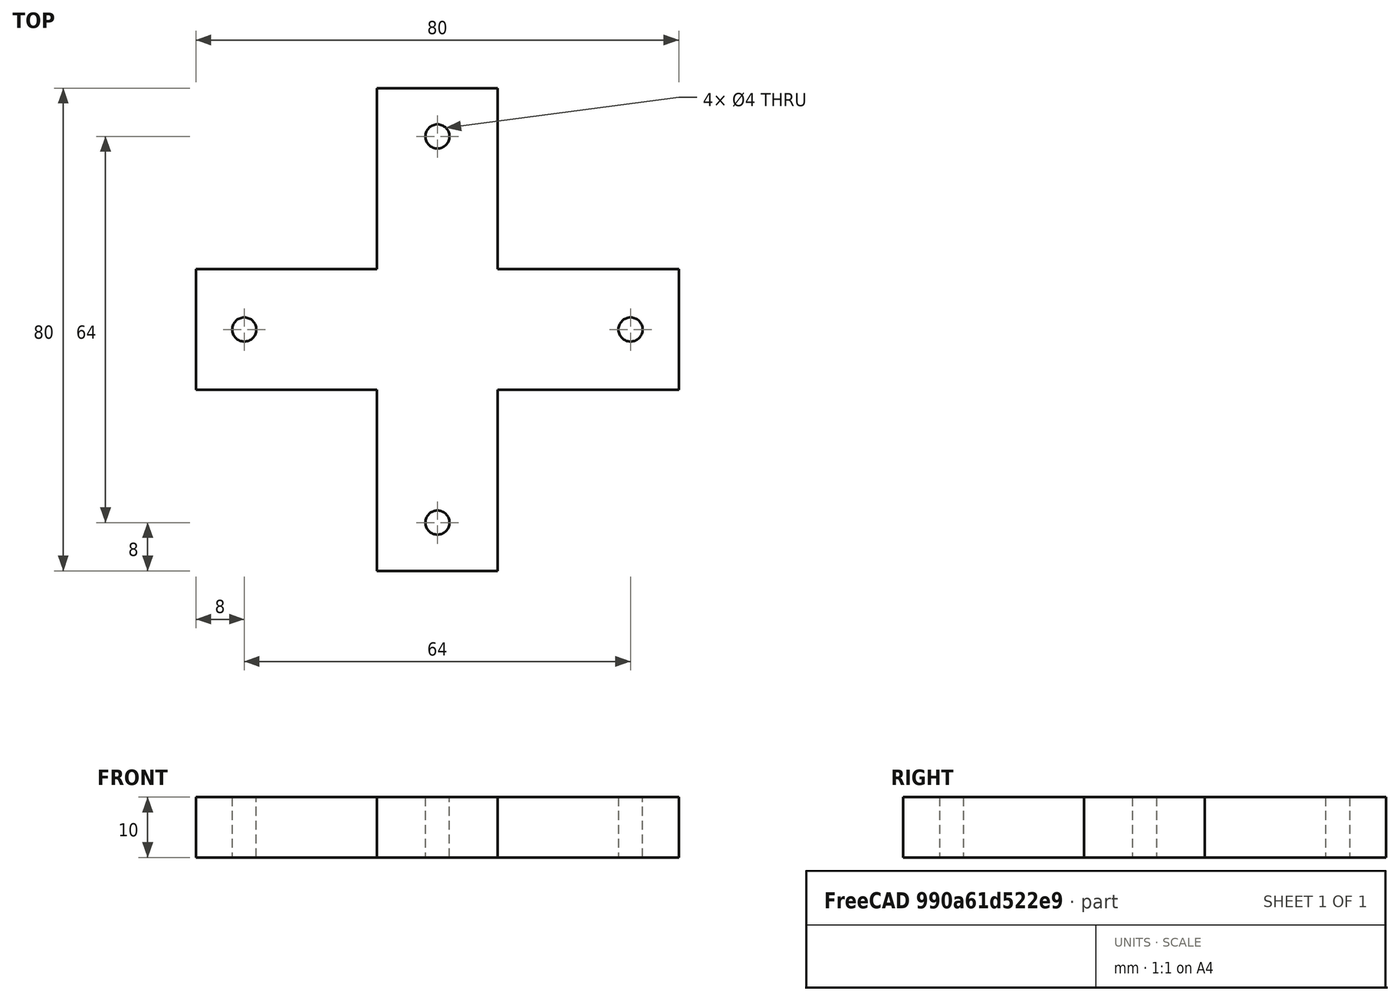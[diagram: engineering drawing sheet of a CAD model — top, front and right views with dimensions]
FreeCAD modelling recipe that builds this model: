
FCSTD DOCUMENT  (FreeCAD 0.21R33694 (Git))
Label: OJT1_T19R02.alf
License: All rights reserved
LicenseURL: http://en.wikipedia.org/wiki/All_rights_reserved
objects: Sketcher::SketchObject×1, PartDesign::Pad×1, PartDesign::Body×1, App::Part×1
note: 4 computed .brp shape members not serialized (recipe doc carries the construction recipe); baked Part::Feature solids carry a one-line shape summary decoded from their .brp

FEATURE [Sketcher::SketchObject] Sketch
  FullyConstrained = true
  MapMode = 5
  Support = -> [XY_Plane001]
  sketch-geometry (16):
    g0: LineSegment StartX=-10 StartY=40 StartZ=0 EndX=10 EndY=40 EndZ=0
    g1: LineSegment StartX=10 StartY=40 StartZ=0 EndX=10 EndY=10 EndZ=0
    g2: LineSegment StartX=10 StartY=10 StartZ=0 EndX=40 EndY=10 EndZ=0
    g3: LineSegment StartX=40 StartY=10 StartZ=0 EndX=40 EndY=-10 EndZ=0
    g4: LineSegment StartX=40 StartY=-10 StartZ=0 EndX=10 EndY=-10 EndZ=0
    g5: LineSegment StartX=10 StartY=-10 StartZ=0 EndX=10 EndY=-40 EndZ=0
    g6: LineSegment StartX=10 StartY=-40 StartZ=0 EndX=-10 EndY=-40 EndZ=0
    g7: LineSegment StartX=-10 StartY=-40 StartZ=0 EndX=-10 EndY=-10 EndZ=0
    g8: LineSegment StartX=-10 StartY=-10 StartZ=0 EndX=-40 EndY=-10 EndZ=0
    g9: LineSegment StartX=-40 StartY=-10 StartZ=0 EndX=-40 EndY=10 EndZ=0
    g10: LineSegment StartX=-40 StartY=10 StartZ=0 EndX=-10 EndY=10 EndZ=0
    g11: LineSegment StartX=-10 StartY=10 StartZ=0 EndX=-10 EndY=40 EndZ=0
    g12: Circle CenterX=0 CenterY=32 CenterZ=0 NormalX=0 NormalY=0 NormalZ=1 AngleXU=0 Radius=2
    g13: Circle CenterX=32 CenterY=0 CenterZ=0 NormalX=0 NormalY=0 NormalZ=1 AngleXU=0 Radius=2
    g14: Circle CenterX=0 CenterY=-32 CenterZ=0 NormalX=0 NormalY=0 NormalZ=1 AngleXU=0 Radius=2
    g15: Circle CenterX=-32 CenterY=0 CenterZ=0 NormalX=0 NormalY=0 NormalZ=1 AngleXU=0 Radius=2
  constraints (45):
    c: Horizontal(g0)
    c: Coincident(g0,g1)
    c: Vertical(g1)
    c: Coincident(g1,g2)
    c: Horizontal(g2)
    c: Coincident(g2,g3)
    c: Vertical(g3)
    c: Coincident(g3,g4)
    c: Coincident(g4,g5)
    c: Vertical(g5)
    c: Coincident(g5,g6)
    c: Horizontal(g6)
    c: Coincident(g6,g7)
    c: Vertical(g7)
    c: Coincident(g7,g8)
    c: Coincident(g8,g9)
    c: Vertical(g9)
    c: Coincident(g9,g10)
    c: Coincident(g10,g11)
    c: Coincident(g11,g0)
    c: Vertical(g11)
    c: Horizontal(g4)
    c: Horizontal(g8)
    c: Horizontal(g10)
    c: Symmetric(g4,g7,g-2)
    c: Distance(g3,g8) = 80
    c: Distance(g6,g5) = 20
    c: Symmetric(g7,g10,g-1)
    c: Symmetric(g10,g1,g-2)
    c: Equal(g11,g10)
    c: Equal(g6,g9)
    c: Equal(g2,g10)
    c: Equal(g10,g7)
    c: PointOnObject(g12,g-2)
    c: Distance(g12,g0) = 8
    c: Diameter(g12) = 4
    c: PointOnObject(g13,g-1)
    c: PointOnObject(g14,g-2)
    c: PointOnObject(g15,g-1)
    c: Distance(g15,g9) = 8
    c: Distance(g14,g6) = 8
    c: Distance(g13,g3) = 8
    c: Diameter(g13) = 4
    c: Diameter(g14) = 4
    c: Diameter(g15) = 4
FEATURE [PartDesign::Pad] Pad
  Direction = (0,0,1)
  Length = 10
  Length2 = 10
  Profile = -> Sketch
  ReferenceAxis = -> Sketch [N_Axis]
  Refine = true
  Type = 0
FEATURE [PartDesign::Body] Body
  Group = -> [Sketch,Pad]
  Origin = -> Origin001
  Tip = -> Pad
FEATURE [App::Part] Part
  Group = -> [Body]
  Origin = -> Origin
